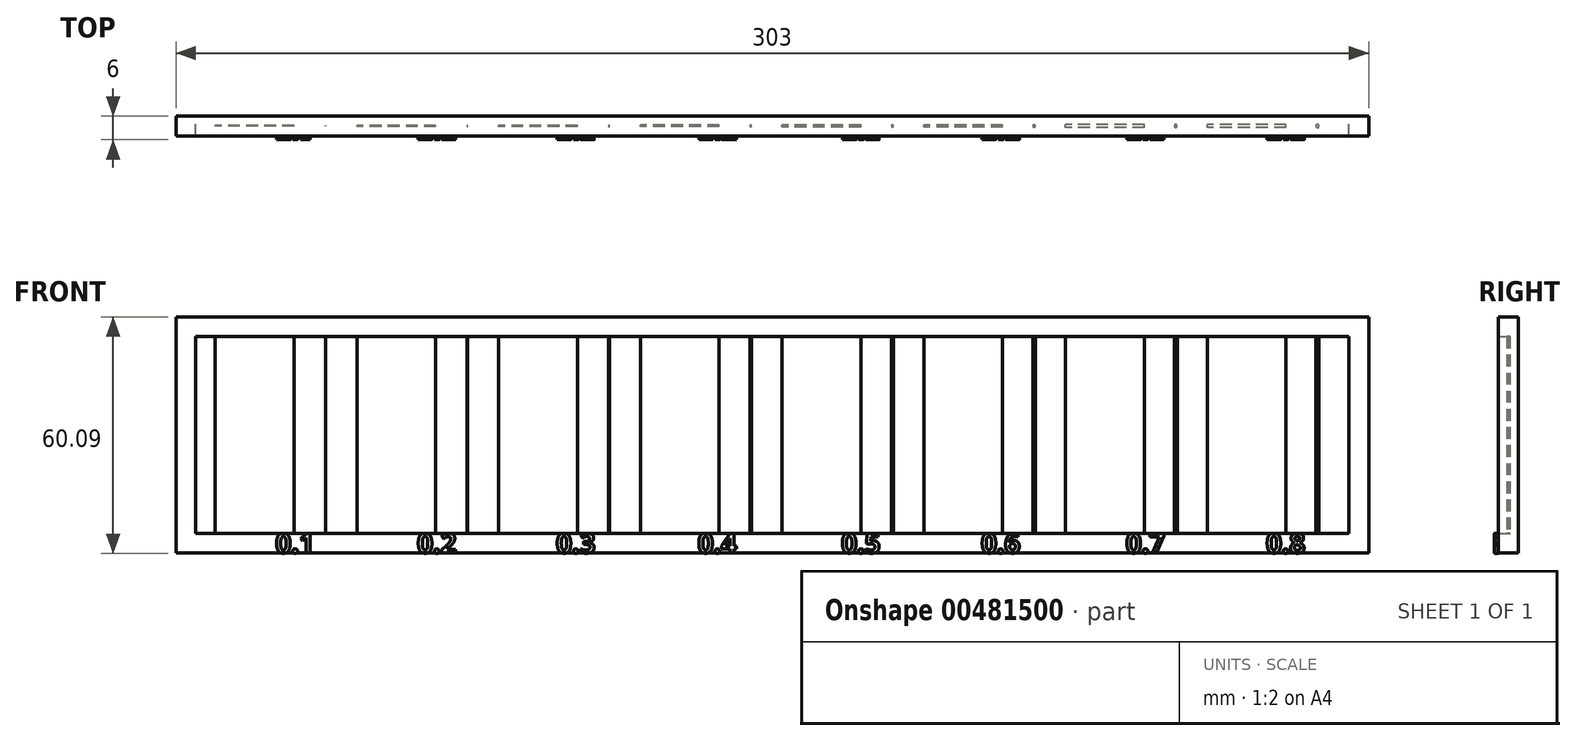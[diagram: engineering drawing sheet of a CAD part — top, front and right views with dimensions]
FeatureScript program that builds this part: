
annotation { "Feature Type Name" : "Feature", "Feature Type Description" : "" }
export const myFeature = defineFeature(function(context is Context, id is Id, definition is map)
    precondition{}
    {
        {
            var Q0;
            Q0=qCreatedBy(makeId("Top.planeOp"),FACE);
            var sketch = newSketch(context, id + "F0", { "sketchPlane" : qUnion([Q0])});
            skLineSegment(sketch, "E0", {"start": v(-91.41, 0) * mm, "end": v(94.52, 0) * mm, "construction": true});
            skLineSegment(sketch, "E1", {"start": v(-84.3, 4.29) * mm, "end": v(-84.3, -4.65) * mm, "construction": true});
            skLineSegment(sketch, "E2.1.0.0", {"start": v(-48.3, 4.29) * mm, "end": v(-48.3, -4.65) * mm, "construction": true});
            skLineSegment(sketch, "E2.2.0.0", {"start": v(-12.3, 4.29) * mm, "end": v(-12.3, -4.65) * mm, "construction": true});
            skLineSegment(sketch, "E2.3.0.0", {"start": v(23.7, 4.29) * mm, "end": v(23.7, -4.65) * mm, "construction": true});
            skLineSegment(sketch, "E2.4.0.0", {"start": v(59.7, 4.29) * mm, "end": v(59.7, -4.65) * mm, "construction": true});
            skLineSegment(sketch, "E2.5.0.0", {"start": v(95.7, 4.29) * mm, "end": v(95.7, -4.65) * mm, "construction": true});
            skLineSegment(sketch, "E2.6.0.0", {"start": v(131.7, 4.29) * mm, "end": v(131.7, -4.65) * mm, "construction": true});
            skLineSegment(sketch, "E2.7.0.0", {"start": v(167.7, 4.29) * mm, "end": v(167.7, -4.65) * mm, "construction": true});
            skLineSegment(sketch, "E2.direction1", {"start": v(-84.3, -4.65) * mm, "end": v(-48.3, -4.65) * mm, "construction": true});
            skLineSegment(sketch, "E3.bottom", {"start": v(-74.3, -0.05) * mm, "end": v(-94.3, -0.05) * mm});
            skLineSegment(sketch, "E3.top", {"start": v(-74.3, 0.05) * mm, "end": v(-94.3, 0.05) * mm});
            skLineSegment(sketch, "E3.left", {"start": v(-74.3, -0.05) * mm, "end": v(-74.3, 0.05) * mm});
            skLineSegment(sketch, "E3.right", {"start": v(-94.3, -0.05) * mm, "end": v(-94.3, 0.05) * mm});
            skPoint(sketch, "E3.middle", {"position": v(-84.3, 0) * mm});
            skLineSegment(sketch, "E4.bottom", {"start": v(-38.3, -0.1) * mm, "end": v(-58.3, -0.1) * mm});
            skLineSegment(sketch, "E4.top", {"start": v(-38.3, 0.1) * mm, "end": v(-58.3, 0.1) * mm});
            skLineSegment(sketch, "E4.left", {"start": v(-38.3, -0.1) * mm, "end": v(-38.3, 0.1) * mm});
            skLineSegment(sketch, "E4.right", {"start": v(-58.3, -0.1) * mm, "end": v(-58.3, 0.1) * mm});
            skPoint(sketch, "E4.middle", {"position": v(-48.3, 0) * mm});
            skLineSegment(sketch, "E5.bottom", {"start": v(69.7, -0.25) * mm, "end": v(49.7, -0.25) * mm});
            skLineSegment(sketch, "E5.top", {"start": v(69.7, 0.25) * mm, "end": v(49.7, 0.25) * mm});
            skLineSegment(sketch, "E5.left", {"start": v(69.7, -0.25) * mm, "end": v(69.7, 0.25) * mm});
            skLineSegment(sketch, "E5.right", {"start": v(49.7, -0.25) * mm, "end": v(49.7, 0.25) * mm});
            skPoint(sketch, "E5.middle", {"position": v(59.7, 0) * mm});
            skLineSegment(sketch, "E6.bottom", {"start": v(105.7, -0.3) * mm, "end": v(85.7, -0.3) * mm});
            skLineSegment(sketch, "E6.top", {"start": v(105.7, 0.3) * mm, "end": v(85.7, 0.3) * mm});
            skLineSegment(sketch, "E6.left", {"start": v(105.7, -0.3) * mm, "end": v(105.7, 0.3) * mm});
            skLineSegment(sketch, "E6.right", {"start": v(85.7, -0.3) * mm, "end": v(85.7, 0.3) * mm});
            skPoint(sketch, "E6.middle", {"position": v(95.7, 0) * mm});
            skLineSegment(sketch, "E7.bottom", {"start": v(141.7, -0.35) * mm, "end": v(121.7, -0.35) * mm});
            skLineSegment(sketch, "E7.top", {"start": v(141.7, 0.35) * mm, "end": v(121.7, 0.35) * mm});
            skLineSegment(sketch, "E7.left", {"start": v(141.7, -0.35) * mm, "end": v(141.7, 0.35) * mm});
            skLineSegment(sketch, "E7.right", {"start": v(121.7, -0.35) * mm, "end": v(121.7, 0.35) * mm});
            skPoint(sketch, "E7.middle", {"position": v(131.7, 0) * mm});
            skLineSegment(sketch, "E8.bottom", {"start": v(177.7, -0.4) * mm, "end": v(157.7, -0.4) * mm});
            skLineSegment(sketch, "E8.top", {"start": v(177.7, 0.4) * mm, "end": v(157.7, 0.4) * mm});
            skLineSegment(sketch, "E8.left", {"start": v(177.7, -0.4) * mm, "end": v(177.7, 0.4) * mm});
            skLineSegment(sketch, "E8.right", {"start": v(157.7, -0.4) * mm, "end": v(157.7, 0.4) * mm});
            skPoint(sketch, "E8.middle", {"position": v(167.7, 0) * mm});
            skLineSegment(sketch, "E9.bottom", {"start": v(-2.3, -0.15) * mm, "end": v(-22.3, -0.15) * mm});
            skLineSegment(sketch, "E9.top", {"start": v(-2.3, 0.15) * mm, "end": v(-22.3, 0.15) * mm});
            skLineSegment(sketch, "E9.left", {"start": v(-2.3, -0.15) * mm, "end": v(-2.3, 0.15) * mm});
            skLineSegment(sketch, "E9.right", {"start": v(-22.3, -0.15) * mm, "end": v(-22.3, 0.15) * mm});
            skPoint(sketch, "E9.middle", {"position": v(-12.3, 0) * mm});
            skLineSegment(sketch, "E10.bottom", {"start": v(33.7, -0.2) * mm, "end": v(13.7, -0.2) * mm});
            skLineSegment(sketch, "E10.top", {"start": v(33.7, 0.2) * mm, "end": v(13.7, 0.2) * mm});
            skLineSegment(sketch, "E10.left", {"start": v(33.7, -0.2) * mm, "end": v(33.7, 0.2) * mm});
            skLineSegment(sketch, "E10.right", {"start": v(13.7, -0.2) * mm, "end": v(13.7, 0.2) * mm});
            skPoint(sketch, "E10.middle", {"position": v(23.7, 0) * mm});
            skLineSegment(sketch, "E11.direction1", {"start": v(-66.3, 0) * mm, "end": v(-36.1, 0) * mm, "construction": true});
            skPoint(sketch, "E12", {"position": v(-66.3, 0) * mm});
            skPoint(sketch, "E13.1.0.0", {"position": v(-30.3, 0) * mm});
            skPoint(sketch, "E13.2.0.0", {"position": v(5.7, 0) * mm});
            skPoint(sketch, "E13.3.0.0", {"position": v(41.7, 0) * mm});
            skPoint(sketch, "E13.4.0.0", {"position": v(77.7, 0) * mm});
            skPoint(sketch, "E13.5.0.0", {"position": v(113.7, 0) * mm});
            skPoint(sketch, "E13.6.0.0", {"position": v(149.7, 0) * mm});
            skPoint(sketch, "E13.7.0.0", {"position": v(185.7, 0) * mm});
            skLineSegment(sketch, "E13.direction1", {"start": v(-66.3, 0) * mm, "end": v(-30.3, 0) * mm, "construction": true});
            skCircle(sketch, "E14", {"center": v(-66.3, 0) * mm, "radius": 0.05 * mm});
            skCircle(sketch, "E15", {"center": v(-30.3, 0) * mm, "radius": 0.1 * mm});
            skCircle(sketch, "E16", {"center": v(5.7, 0) * mm, "radius": 0.15 * mm});
            skCircle(sketch, "E17", {"center": v(41.7, 0) * mm, "radius": 0.2 * mm});
            skCircle(sketch, "E18", {"center": v(77.7, 0) * mm, "radius": 0.25 * mm});
            skCircle(sketch, "E19", {"center": v(113.7, 0) * mm, "radius": 0.3 * mm});
            skCircle(sketch, "E20", {"center": v(149.7, 0) * mm, "radius": 0.35 * mm});
            skCircle(sketch, "E21", {"center": v(185.7, 0) * mm, "radius": 0.4 * mm});
            skSolve(sketch);
        }
        {
            var Q0;
            Q0 = qSketchRegion(id + "F0", true);
            extrude(context, id + "F1", {"entities" : qUnion([Q0]), "depth" : 50 * mm});
        }
        {
            var Q0;
            Q0=qCreatedBy(makeId("Front.planeOp"),FACE);
            var sketch = newSketch(context, id + "F2", { "sketchPlane" : qUnion([Q0])});
            skLineSegment(sketch, "E22.bottom", {"start": v(-99.3, 0) * mm, "end": v(193.7, 0) * mm});
            skLineSegment(sketch, "E22.top", {"start": v(-99.3, 50) * mm, "end": v(193.7, 50) * mm});
            skLineSegment(sketch, "E22.left", {"start": v(-99.3, 0) * mm, "end": v(-99.3, 50) * mm});
            skLineSegment(sketch, "E22.right", {"start": v(193.7, 0) * mm, "end": v(193.7, 50) * mm});
            skLineSegment(sketch, "E23.0", {"start": v(-104.3, -5) * mm, "end": v(-104.3, 55) * mm});
            skLineSegment(sketch, "E23.1", {"start": v(-104.3, -5) * mm, "end": v(198.7, -5) * mm});
            skLineSegment(sketch, "E23.2", {"start": v(198.7, -5) * mm, "end": v(198.7, 55) * mm});
            skLineSegment(sketch, "E23.3", {"start": v(-104.3, 55) * mm, "end": v(198.7, 55) * mm});
            skSolve(sketch);
        }
        {
            var Q0;
            Q0 = qSketchRegion(id + "F2", true);
            extrude(context, id + "F3", {"entities" : qUnion([Q0]), "depth" : 2.5 * mm, "hasSecondDirection" : true, "secondDirectionOppositeDirection" : true, "secondDirectionDepth" : 2.5 * mm});
        }
        {
            var Q0;
            Q0=makeQuery(id+"F3.opExtrude","CAP_FACE",FACE,{"disambiguationData":[OSD([sQuery(id+"F2.wireOp",EDGE,"E22.bottom"),sQuery(id+"F2.wireOp",EDGE,"E22.top"),sQuery(id+"F2.wireOp",EDGE,"E22.left"),sQuery(id+"F2.wireOp",EDGE,"E22.right"),sQuery(id+"F2.wireOp",EDGE,"E23.0"),sQuery(id+"F2.wireOp",EDGE,"E23.1"),sQuery(id+"F2.wireOp",EDGE,"E23.2"),sQuery(id+"F2.wireOp",EDGE,"E23.3")])],"isStart":false});
            var sketch = newSketch(context, id + "F4", { "sketchPlane" : qUnion([Q0])});
            skText(sketch, "E24", { "text": "0.1", "fontName": "OpenSans-Bold.ttf"});
            skText(sketch, "E25", { "text": "0.2", "fontName": "OpenSans-Bold.ttf"});
            skText(sketch, "E26", { "text": "0.3", "fontName": "OpenSans-Bold.ttf"});
            skText(sketch, "E27", { "text": "0.4\n", "fontName": "OpenSans-Bold.ttf"});
            skText(sketch, "E28", { "text": "0.5", "fontName": "OpenSans-Bold.ttf"});
            skText(sketch, "E29", { "text": "0.6", "fontName": "OpenSans-Bold.ttf"});
            skText(sketch, "E30", { "text": "0.7", "fontName": "OpenSans-Bold.ttf"});
            skText(sketch, "E31", { "text": "0.8", "fontName": "OpenSans-Bold.ttf"});
            const initialGuessF4  = {"E24": [-0.079, -0.005, 1, 0, 0.005], "E25": [-0.043, -0.005, 1, 0, 0.005], "E26": [-0.0077, -0.005, 1, 0, 0.005], "E27": [0.02827, -0.005, 1, 0, 0.005], "E28": [0.06474, -0.005, 1, 0, 0.005], "E29": [0.10026, -0.005, 1, 0, 0.005], "E30": [0.13703, -0.005, 1, 0, 0.005], "E31": [0.17265, -0.005, 1, 0, 0.005]};
            skSetInitialGuess(sketch, initialGuessF4);
            skSolve(sketch);
        }
        {
            var Q0;
            Q0 = qSketchRegion(id + "F4", true);
            extrude(context, id + "F5", {"entities" : qUnion([Q0]), "operationType" : NewBodyOperationType.ADD, "depth" : 1 * mm});
        }
    });
